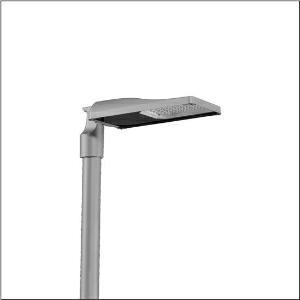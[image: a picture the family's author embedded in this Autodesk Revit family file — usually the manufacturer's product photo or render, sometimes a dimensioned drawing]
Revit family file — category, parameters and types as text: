
# Revit family: streetlight_sl_31_mini___st1_0a_5xh2d3aa08ja_eb00
name_source: partatom
category: Lighting Fixtures
units: mm (PartAtom-declared; Revit-internal decimal feet)

## family parameters
Cut with Voids When Loaded = No
Host = Face
Light Source = No
Part Type = Normal
Room Calculation Point = No
Round Connector Dimension = Use Diameter
Shared = No

## types (1)
- --- (1 x LED, 12140 lm, 81.1 W, 3000K)
    Apparent Load = 81 VA
    CIE Flux Codes = 40 73 97 100 100
    Color Rendering = 70
    Color Temperature = 3000K
    Default Elevation = 1800 mm
    Description = Streetlight SL 31 mini, mast luminaire, primary light control with lens, of PMMA, primary optical cover: cover, of toughened safety glass, transparent, light distribution: ST1.0a, light emission: direct distribution, primary light characteristic: asymmetric, installation type: post-top, side-entry, LED, High Power LED, rated luminous flux: 12.140lm, luminous efficacy: 150lm/W, light colour: 730, colour temperature: 3000K, control: overheat protection, intelligent temperature release in ECG and LED module, constant luminous flux control, time-dependent luminous flux control, flexible luminous flux parameterisation, presetting dimming linear, with cable H07RN-F 2x 1.5mm², mains connection: 220..240V, AC, 50/60Hz, connection cable pre-assembled, cable length: 10,5m, start of lifetime: 81W, end of service life: 88W, reduction: 36W, luminaire housing, of diecast aluminium, powder-coated, Siteco® metallic grey (DB 702S), corrosivity category C5 high according to DIN EN ISO 12944, no sealing on luminaire upper side, inclination: -15°..+20° (post-top) | -20°..+20° (side-entry), adjustable in 5° steps, mast flange (76/60mm) included as standard, multi-level sealing system, sealing non-destructively replaceable, protection rating (complete): IP66, insulation class (complete): insulation class II (safety insulation), certification: CE, ENEC, ENEC+, VDE, UKCA, impact resistance: IK09, permissible operating ambient temperature for outdoor applications: -40..+50°C, standard-compliant lighting for roads and squares, packaging unit: 1 piece

Light Distribution: ST1.0a
    Height = 76 mm
    Lamp = 1 x LED
    Lamp Light Flux = 12140 lm
    Lamp Power = 81.1 W
    Lamp count = 1
    Length = 547 mm
    Luminous efficacy = 150 lm/W
    Manufacturer = Siteco
    ModVariant = No
    Model = 5XH2D3AA08JA
    Number of Poles = 1
    OnlyDefault = Yes
    Power Factor = 1
    Product Name = Streetlight SL 31 mini | ST1.0a
    Product group = mast luminaire | pylon top
    ProductGroupID = 6100
    Protection Class = Protection class II
    Protection Degree = IP 66
    RLX_Detail_Level = 1
    RLX_Emergency_Light_Flux = 0 lm
    RLX_Emergency_Type = 0
    RLX_Emergency_Type_DB = No
    RlxData = <blob elided: 39945 chars, md5=2e80cfdd>
    Socket = socket
    Standby Power = 0 W
    System Light Flux = 12140 lm
    System Power = 81 W
    Type Comments = factory setting: luminous flux: 100 % | dim-lin: 254 | 860 mA
    Type Image = l_1300326.jpg
    URL = http://relux.com
    VarID = @adj_008735
    Voltage = 0 V
    Weight = 0.00 kg
    Width = 265 mm

## geometry (parser evidence)
native form markers: Blend x4, Sweep x9
no freeform markers — native parametric forms only
